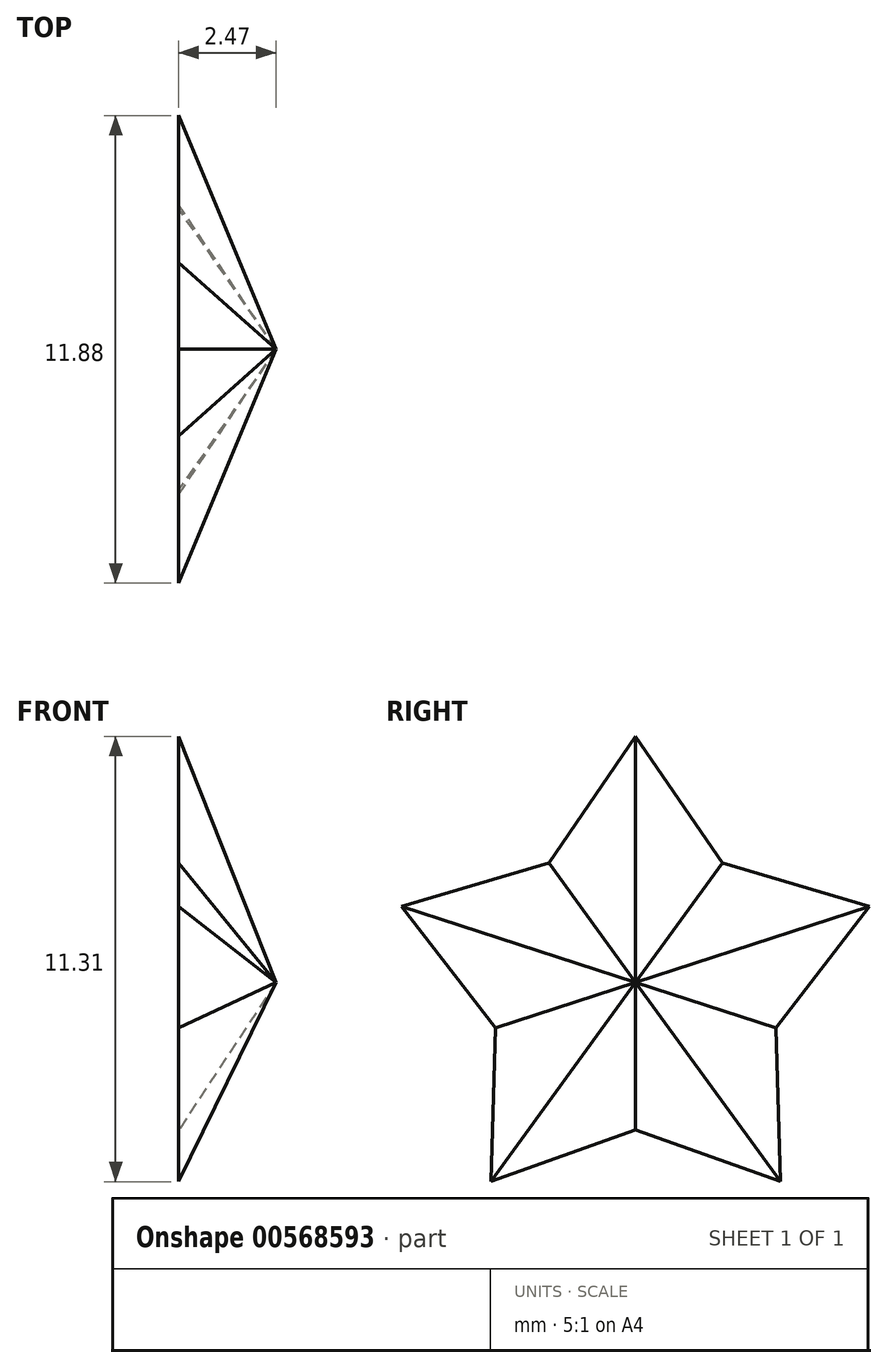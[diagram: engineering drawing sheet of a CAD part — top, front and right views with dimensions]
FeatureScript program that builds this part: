
annotation { "Feature Type Name" : "Feature", "Feature Type Description" : "" }
export const myFeature = defineFeature(function(context is Context, id is Id, definition is map)
    precondition{}
    {
        {
            var Q0;
            Q0=qCreatedBy(makeId("Right.planeOp"),FACE);
            var sketch = newSketch(context, id + "F0", { "sketchPlane" : qUnion([Q0])});
            skLineSegment(sketch, "E0", {"start": v(-5.94, 1.93) * mm, "end": v(-3.57, -1.16) * mm});
            skLineSegment(sketch, "E1", {"start": v(-3.57, -1.16) * mm, "end": v(-3.67, -5.06) * mm});
            skLineSegment(sketch, "E2", {"start": v(-3.67, -5.06) * mm, "end": v(0, -3.75) * mm});
            skLineSegment(sketch, "E3", {"start": v(0, -3.75) * mm, "end": v(3.67, -5.06) * mm});
            skLineSegment(sketch, "E4", {"start": v(3.67, -5.06) * mm, "end": v(3.57, -1.16) * mm});
            skLineSegment(sketch, "E5", {"start": v(3.57, -1.16) * mm, "end": v(5.94, 1.93) * mm});
            skLineSegment(sketch, "E6", {"start": v(5.94, 1.93) * mm, "end": v(2.2, 3.03) * mm});
            skLineSegment(sketch, "E7", {"start": v(2.2, 3.03) * mm, "end": v(0, 6.25) * mm});
            skLineSegment(sketch, "E8", {"start": v(0, 6.25) * mm, "end": v(-2.2, 3.03) * mm});
            skLineSegment(sketch, "E9", {"start": v(-2.2, 3.03) * mm, "end": v(-5.94, 1.93) * mm});
            skLineSegment(sketch, "E10", {"start": v(-3.67, -5.06) * mm, "end": v(0, 0) * mm});
            skLineSegment(sketch, "E11", {"start": v(0, 0) * mm, "end": v(3.67, -5.06) * mm});
            skLineSegment(sketch, "E12", {"start": v(0, 0) * mm, "end": v(5.94, 1.93) * mm});
            skLineSegment(sketch, "E13", {"start": v(0, 0) * mm, "end": v(0, 6.25) * mm});
            skLineSegment(sketch, "E14", {"start": v(0, 0) * mm, "end": v(-5.94, 1.93) * mm});
            skLineSegment(sketch, "E15", {"start": v(0, 0) * mm, "end": v(3.57, -1.16) * mm});
            skLineSegment(sketch, "E16", {"start": v(0, 0) * mm, "end": v(2.2, 3.03) * mm});
            skLineSegment(sketch, "E17", {"start": v(0, 0) * mm, "end": v(-2.2, 3.03) * mm});
            skLineSegment(sketch, "E18", {"start": v(0, 0) * mm, "end": v(-3.57, -1.16) * mm});
            skLineSegment(sketch, "E19", {"start": v(0, 0) * mm, "end": v(0, -3.75) * mm});
            skSolve(sketch);
        }
        {
            var Q0;
            Q0=qSketchRegion(id+"F0",true);
            extrude(context, id + "F1", {"entities" : qUnion([Q0]), "depth" : 4 * mm, "offsetDistance" : 25 * mm, "hasDraft" : true, "draftAngle" : 55 * degree, "draftPullDirection" : true});
        }
    });
